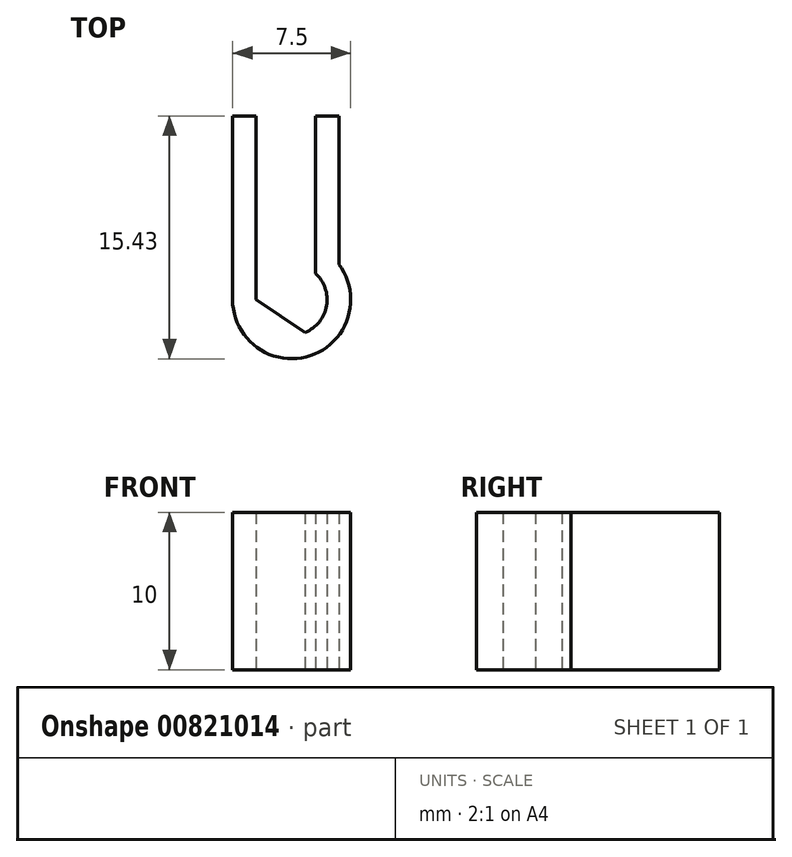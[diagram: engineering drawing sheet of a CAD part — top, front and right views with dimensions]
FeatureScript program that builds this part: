
annotation { "Feature Type Name" : "Feature", "Feature Type Description" : "" }
export const myFeature = defineFeature(function(context is Context, id is Id, definition is map)
    precondition{}
    {
        {
            var Q0;
            Q0=qCreatedBy(makeId("Top.planeOp"),FACE);
            var sketch = newSketch(context, id + "F0", { "sketchPlane" : qUnion([Q0])});
            skCircle(sketch, "E0", {"center": v(0, 0) * mm, "radius": 2.25 * mm});
            skLineSegment(sketch, "E1", {"start": v(-2.25, 0) * mm, "end": v(-2.25, 11.68) * mm});
            skLineSegment(sketch, "E2", {"start": v(1.5, 1.68) * mm, "end": v(1.5, 11.68) * mm});
            skCircle(sketch, "E3", {"center": v(0, 0) * mm, "radius": 3.75 * mm});
            skLineSegment(sketch, "E4", {"start": v(-3.75, 0) * mm, "end": v(-3.75, 11.68) * mm});
            skLineSegment(sketch, "E5", {"start": v(3, 2.25) * mm, "end": v(3, 11.68) * mm});
            skLineSegment(sketch, "E6", {"start": v(-3.75, 11.68) * mm, "end": v(-2.25, 11.68) * mm});
            skLineSegment(sketch, "E7", {"start": v(1.5, 11.68) * mm, "end": v(3, 11.68) * mm});
            skLineSegment(sketch, "E8", {"start": v(-2.25, 0) * mm, "end": v(0.86, -2.08) * mm});
            skSolve(sketch);
        }
        {
            var Q0;
            {var subQ4=sQuery(id+"F0.wireOp",EDGE,"E4");Q0=makeQuery(id+"F0.imprint","IMPRINT",FACE,{"disambiguationData":[TD([[makeQuery(id+"F0.imprint","IMPRINT",EDGE,{"derivedFrom":subQ4}),-1.0]])]});}
            var Q1;
            {var subQ1=sQuery(id+"F0.wireOp",EDGE,"E0");var subQ5=sQuery(id+"F0.wireOp",EDGE,"E1");var subQ6=makeQuery(id+"F0.imprint","INTERSECT",VERTEX,{"derivedFrom":[subQ1,subQ5]});Q1=makeQuery(id+"F0.imprint","IMPRINT",FACE,{"disambiguationData":[TD([[makeQuery(id+"F0.imprint","IMPRINT",EDGE,{"disambiguationData":[TD([[subQ6,-1.0]])],"derivedFrom":subQ1}),-1.0]])]});}
            var Q2;
            {var subQ4=sQuery(id+"F0.wireOp",EDGE,"E5");Q2=makeQuery(id+"F0.imprint","IMPRINT",FACE,{"disambiguationData":[TD([[makeQuery(id+"F0.imprint","IMPRINT",EDGE,{"derivedFrom":subQ4}),1.0]])]});}
            var Q3;
            {var subQ0=sQuery(id+"F0.wireOp",EDGE,"sSwPKtTy-Yggn-ZSeM-zrsy-cesaZOwxugov");Q3=makeQuery(id+"F0.imprint","IMPRINT",FACE,{"disambiguationData":[TD([[makeQuery(id+"F0.imprint","IMPRINT",EDGE,{"derivedFrom":subQ0}),-1.0]])]});}
            var Q4;
            {var subQ0=sQuery(id+"F0.wireOp",EDGE,"E8");Q4=makeQuery(id+"F0.imprint","IMPRINT",FACE,{"disambiguationData":[TD([[makeQuery(id+"F0.imprint","IMPRINT",EDGE,{"derivedFrom":subQ0}),-1.0]])]});}
            extrude(context, id + "F1", {"entities" : qUnion([Q0, Q1, Q2, Q3, Q4]), "depth" : 10 * mm, "offsetDistance" : 25 * mm});
        }
    });
